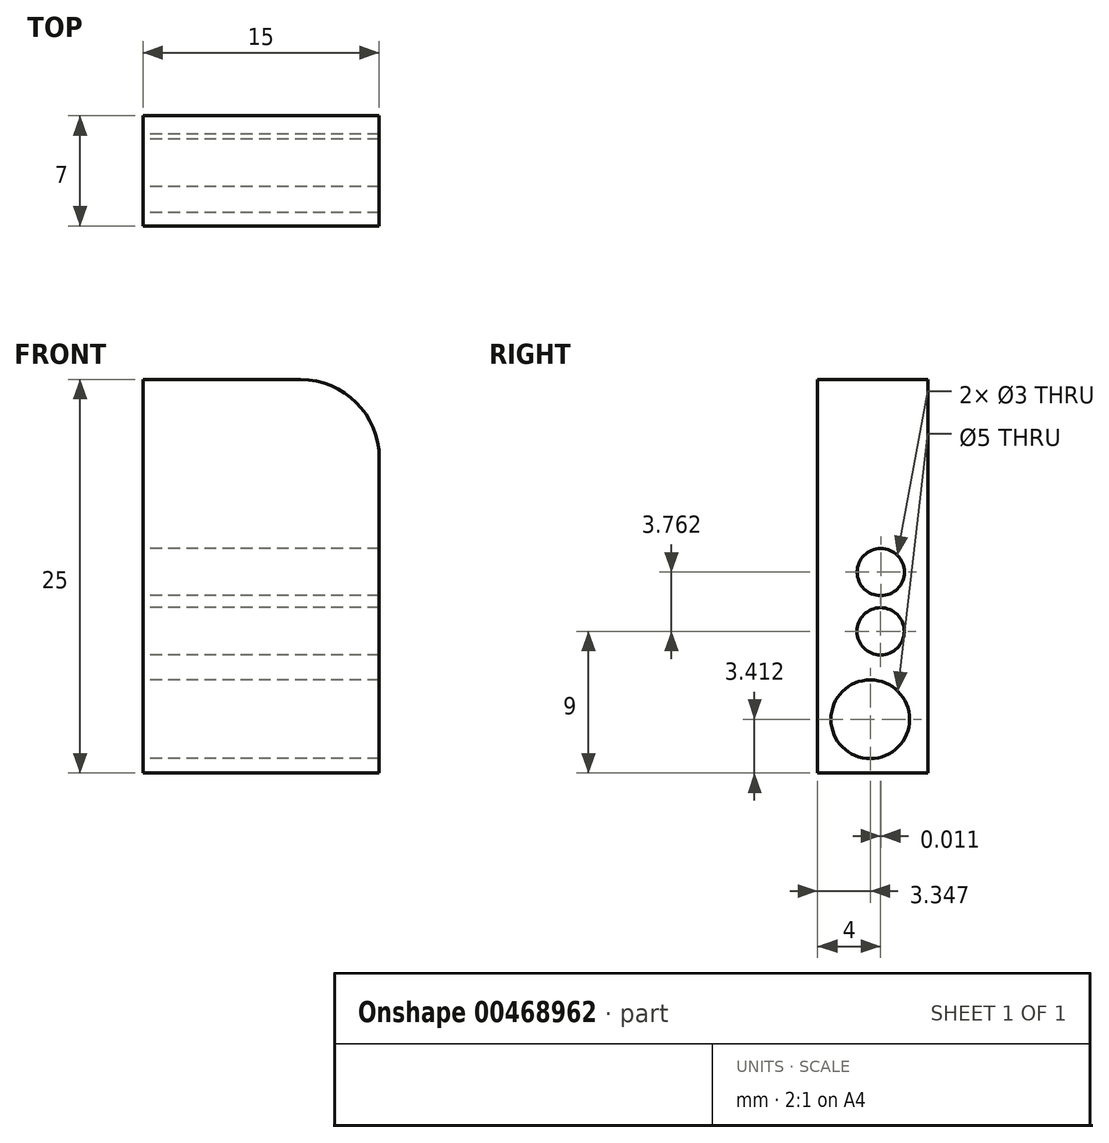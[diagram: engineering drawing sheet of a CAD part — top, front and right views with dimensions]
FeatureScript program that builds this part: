
annotation { "Feature Type Name" : "Feature", "Feature Type Description" : "" }
export const myFeature = defineFeature(function(context is Context, id is Id, definition is map)
    precondition{}
    {
        {
            var Q0;
            Q0=qCreatedBy(makeId("Front.planeOp"),FACE);
            var sketch = newSketch(context, id + "F0", { "sketchPlane" : qUnion([Q0])});
            skLineSegment(sketch, "E0.bottom", {"start": v(0, 0) * mm, "end": v(10, 0) * mm});
            skLineSegment(sketch, "E0.top", {"start": v(0, -25) * mm, "end": v(15, -25) * mm});
            skLineSegment(sketch, "E0.left", {"start": v(0, 0) * mm, "end": v(0, -25) * mm});
            skLineSegment(sketch, "E0.right", {"start": v(15, -5) * mm, "end": v(15, -25) * mm});
            skPoint(sketch, "E1.visualSharp", {"position": v(15, 0) * mm});
            skArc(sketch, "E1.filletArc", {"start": v(15, -5) * mm, "mid": v(13.54, -1.46) * mm, "end": v(10, 0) * mm});
            skSolve(sketch);
        }
        {
            var Q0;
            Q0=makeQuery(id+"F0.imprint","IMPRINT",FACE,{"disambiguationData":[TD([[makeQuery(id+"F0.imprint","IMPRINT",EDGE,{"derivedFrom":sQuery(id+"F0.wireOp",EDGE,"E0.bottom")}),-1.0]])]});
            extrude(context, id + "F1", {"entities" : qUnion([Q0]), "depth" : 7 * mm, "offsetDistance" : 25 * mm});
        }
        {
            var Q0;
            Q0=makeQuery(id+"F1.opExtrude","SWEPT_FACE",FACE,{"disambiguationData":[OSD([sQuery(id+"F0.wireOp",EDGE,"E0.left")])]});
            var sketch = newSketch(context, id + "F2", { "sketchPlane" : qUnion([Q0])});
            skCircle(sketch, "E2", {"center": v(2.99, -12.24) * mm, "radius": 1.5 * mm});
            skCircle(sketch, "E3", {"center": v(3, -16) * mm, "radius": 1.5 * mm});
            skCircle(sketch, "E4", {"center": v(3.65, -21.59) * mm, "radius": 2.5 * mm});
            skSolve(sketch);
        }
        {
            var Q0;
            Q0=makeQuery(id+"F2.imprint","IMPRINT",FACE,{"disambiguationData":[TD([[makeQuery(id+"F2.imprint","IMPRINT",EDGE,{"derivedFrom":sQuery(id+"F2.wireOp",EDGE,"E2")}),1.0]])]});
            var Q1;
            Q1=makeQuery(id+"F2.imprint","IMPRINT",FACE,{"disambiguationData":[TD([[makeQuery(id+"F2.imprint","IMPRINT",EDGE,{"derivedFrom":sQuery(id+"F2.wireOp",EDGE,"E3")}),1.0]])]});
            var Q2;
            Q2=makeQuery(id+"F2.imprint","IMPRINT",FACE,{"disambiguationData":[TD([[makeQuery(id+"F2.imprint","IMPRINT",EDGE,{"derivedFrom":sQuery(id+"F2.wireOp",EDGE,"E4")}),1.0]])]});
            extrude(context, id + "F3", {"entities" : qUnion([Q0, Q1, Q2]), "operationType" : NewBodyOperationType.REMOVE, "oppositeDirection" : true, "depth" : 20 * mm, "offsetDistance" : 25 * mm});
        }
    });
